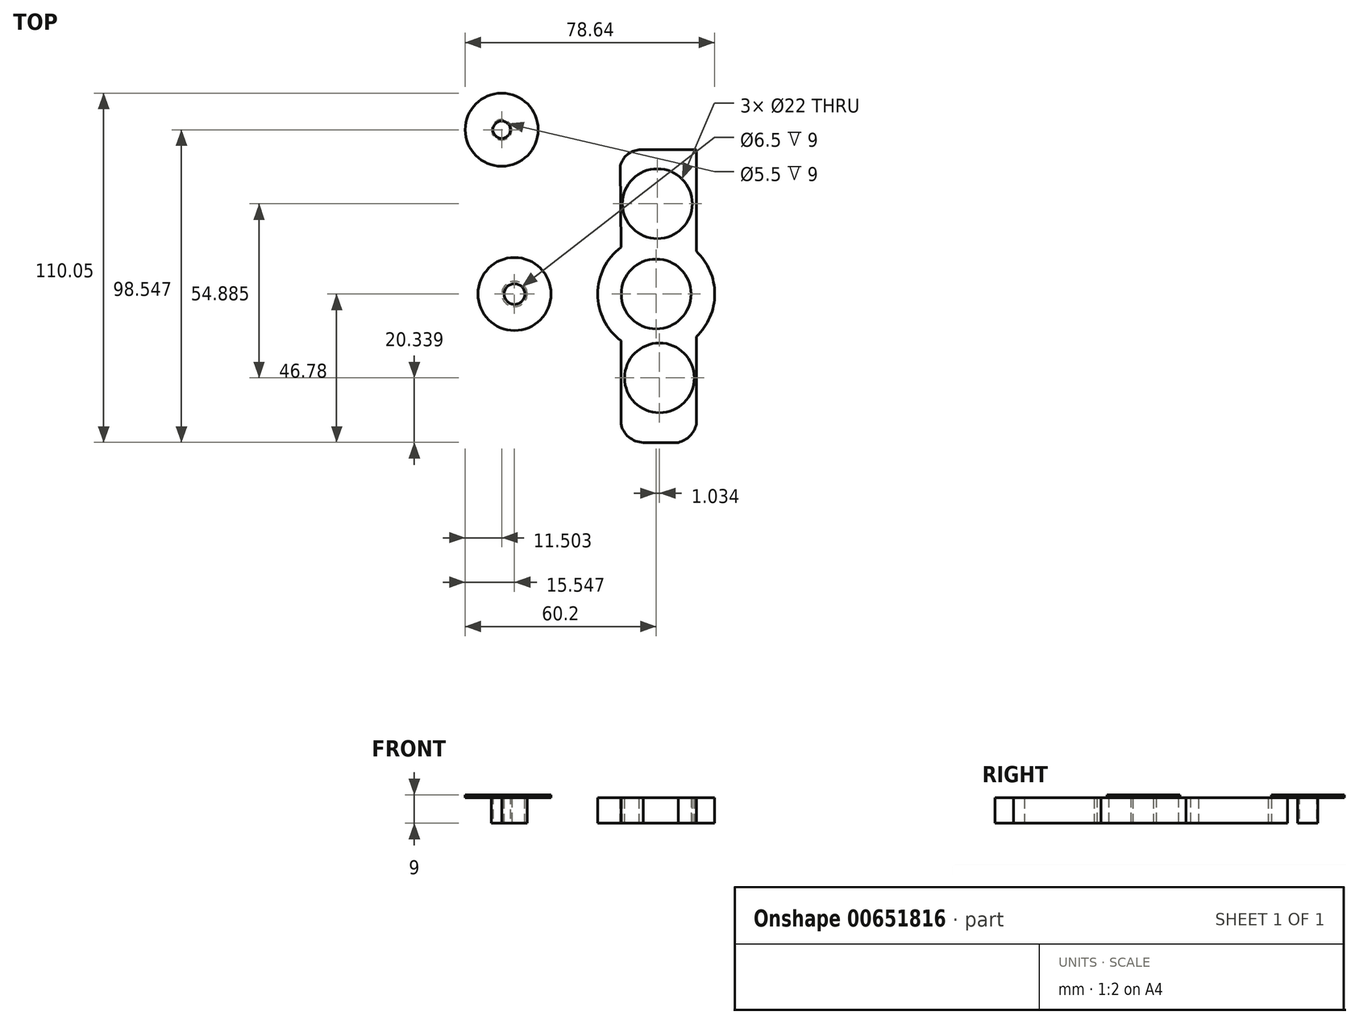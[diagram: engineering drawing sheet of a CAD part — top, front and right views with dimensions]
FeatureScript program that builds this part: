
annotation { "Feature Type Name" : "Feature", "Feature Type Description" : "" }
export const myFeature = defineFeature(function(context is Context, id is Id, definition is map)
    precondition{}
    {
        {
            var Q0;
            Q0=qCreatedBy(makeId("Top.planeOp"),FACE);
            var sketch = newSketch(context, id + "F0", { "sketchPlane" : qUnion([Q0])});
            skCircle(sketch, "E0", {"center": v(0, 0) * mm, "radius": 11 * mm});
            skCircle(sketch, "E1", {"center": v(0, 0) * mm, "radius": 18.44 * mm});
            skLineSegment(sketch, "E2", {"start": v(-11.12, 14.72) * mm, "end": v(-11.36, 45.43) * mm});
            skLineSegment(sketch, "E3", {"start": v(-11.36, 45.43) * mm, "end": v(12.64, 45.43) * mm});
            skLineSegment(sketch, "E4", {"start": v(12.64, 45.43) * mm, "end": v(12.64, 13.43) * mm});
            skLineSegment(sketch, "E5", {"start": v(-11.12, -14.72) * mm, "end": v(-11.12, -46.78) * mm});
            skLineSegment(sketch, "E6", {"start": v(12.64, -13.43) * mm, "end": v(12.64, -46.78) * mm});
            skLineSegment(sketch, "E7", {"start": v(12.64, -46.78) * mm, "end": v(-11.12, -46.78) * mm});
            skSolve(sketch);
        }
        {
            var Q0;
            {var subQ0=sQuery(id+"F0.wireOp",EDGE,"E2");Q0=makeQuery(id+"F0.imprint","IMPRINT",FACE,{"disambiguationData":[TD([[makeQuery(id+"F0.imprint","IMPRINT",EDGE,{"derivedFrom":subQ0}),-1.0]])]});}
            var Q1;
            Q1=makeQuery(id+"F0.imprint","IMPRINT",FACE,{"disambiguationData":[TD([[makeQuery(id+"F0.imprint","IMPRINT",EDGE,{"derivedFrom":sQuery(id+"F0.wireOp",EDGE,"E0")}),-1.0]])]});
            var Q2;
            {var subQ0=sQuery(id+"F0.wireOp",EDGE,"E5");Q2=makeQuery(id+"F0.imprint","IMPRINT",FACE,{"disambiguationData":[TD([[makeQuery(id+"F0.imprint","IMPRINT",EDGE,{"derivedFrom":subQ0}),1.0]])]});}
            extrude(context, id + "F1", {"entities" : qUnion([Q0, Q1, Q2]), "depth" : 8 * mm});
        }
        {
            var Q0;
            Q0=makeQuery(id+"F1.opExtrude","CAP_FACE",FACE,{"disambiguationData":[OSD([sQuery(id+"F0.wireOp",EDGE,"E0"),sQuery(id+"F0.wireOp",EDGE,"E1"),sQuery(id+"F0.wireOp",EDGE,"E2"),sQuery(id+"F0.wireOp",EDGE,"E3"),sQuery(id+"F0.wireOp",EDGE,"E4"),sQuery(id+"F0.wireOp",EDGE,"E5"),sQuery(id+"F0.wireOp",EDGE,"E6"),sQuery(id+"F0.wireOp",EDGE,"E7")])],"isStart":false});
            var sketch = newSketch(context, id + "F2", { "sketchPlane" : qUnion([Q0])});
            skArc(sketch, "E8", {"start": v(-11.12, -37.97) * mm, "mid": v(-9.67, -44) * mm, "end": v(-4.13, -46.78) * mm});
            skArc(sketch, "E9", {"start": v(6.95, -46.78) * mm, "mid": v(11.59, -43.53) * mm, "end": v(12.64, -37.97) * mm});
            skArc(sketch, "E10", {"start": v(12.64, 37.03) * mm, "mid": v(11.6, 43.27) * mm, "end": v(5.64, 45.43) * mm});
            skArc(sketch, "E11", {"start": v(-4.13, 45.43) * mm, "mid": v(-9.92, 43.1) * mm, "end": v(-11.36, 37.03) * mm});
            skSolve(sketch);
        }
        {
            var Q0;
            {var subQ0=sQuery(id+"F2.wireOp",EDGE,"E11");var subQ1=makeQuery(id+"F1.opExtrude","CAP_EDGE",EDGE,{"disambiguationData":[OSD([sQuery(id+"F0.wireOp",EDGE,"E2")])],"isStart":false});var subQ2=makeQuery(id+"F2.imprint","INTERSECT",VERTEX,{"derivedFrom":[subQ1,subQ0]});Q0=makeQuery(id+"F2.imprint","IMPRINT",FACE,{"disambiguationData":[TD([[makeQuery(id+"F2.imprint","IMPRINT",EDGE,{"disambiguationData":[TD([[subQ2,1.0]])],"derivedFrom":subQ0}),-1.0]])]});}
            var Q1;
            {var subQ0=sQuery(id+"F2.wireOp",EDGE,"E10");var subQ1=makeQuery(id+"F1.opExtrude","CAP_EDGE",EDGE,{"disambiguationData":[OSD([sQuery(id+"F0.wireOp",EDGE,"E4")])],"isStart":false});var subQ2=makeQuery(id+"F2.imprint","INTERSECT",VERTEX,{"disambiguationData":[OD(1.0)],"derivedFrom":[subQ1,subQ0]});Q1=makeQuery(id+"F2.imprint","IMPRINT",FACE,{"disambiguationData":[TD([[makeQuery(id+"F2.imprint","IMPRINT",EDGE,{"disambiguationData":[TD([[subQ2,-1.0]])],"derivedFrom":subQ0}),-1.0]])]});}
            var Q2;
            {var subQ0=sQuery(id+"F2.wireOp",EDGE,"E8");var subQ1=makeQuery(id+"F1.opExtrude","CAP_EDGE",EDGE,{"disambiguationData":[OSD([sQuery(id+"F0.wireOp",EDGE,"E7")])],"isStart":false});var subQ2=makeQuery(id+"F2.imprint","INTERSECT",VERTEX,{"derivedFrom":[subQ1,subQ0]});Q2=makeQuery(id+"F2.imprint","IMPRINT",FACE,{"disambiguationData":[TD([[makeQuery(id+"F2.imprint","IMPRINT",EDGE,{"disambiguationData":[TD([[subQ2,1.0]])],"derivedFrom":subQ0}),-1.0]])]});}
            var Q3;
            {var subQ0=sQuery(id+"F2.wireOp",EDGE,"E9");var subQ1=makeQuery(id+"F1.opExtrude","CAP_EDGE",EDGE,{"disambiguationData":[OSD([sQuery(id+"F0.wireOp",EDGE,"E7")])],"isStart":false});var subQ2=makeQuery(id+"F2.imprint","INTERSECT",VERTEX,{"derivedFrom":[subQ1,subQ0]});Q3=makeQuery(id+"F2.imprint","IMPRINT",FACE,{"disambiguationData":[TD([[makeQuery(id+"F2.imprint","IMPRINT",EDGE,{"disambiguationData":[TD([[subQ2,-1.0]])],"derivedFrom":subQ0}),-1.0]])]});}
            extrude(context, id + "F3", {"entities" : qUnion([Q0, Q1, Q2, Q3]), "operationType" : NewBodyOperationType.REMOVE, "oppositeDirection" : true, "depth" : 25 * mm});
        }
        {
            var Q0;
            Q0=qCreatedBy(makeId("Top.planeOp"),FACE);
            var sketch = newSketch(context, id + "F4", { "sketchPlane" : qUnion([Q0])});
            skCircle(sketch, "E12", {"center": v(-44.65, 0) * mm, "radius": 4 * mm});
            skSolve(sketch);
        }
        {
            var Q0;
            Q0=makeQuery(id+"F4.imprint","IMPRINT",FACE,{"disambiguationData":[TD([[makeQuery(id+"F4.imprint","IMPRINT",EDGE,{"derivedFrom":sQuery(id+"F4.wireOp",EDGE,"E12")}),1.0]])]});
            extrude(context, id + "F5", {"entities" : qUnion([Q0]), "depth" : 8 * mm});
        }
        {
            var Q0;
            Q0=makeQuery(id+"F5.opExtrude","CAP_FACE",FACE,{"disambiguationData":[OSD([sQuery(id+"F4.wireOp",EDGE,"E12")])],"isStart":false});
            var sketch = newSketch(context, id + "F6", { "sketchPlane" : qUnion([Q0])});
            skCircle(sketch, "E13", {"center": v(-44.65, 0) * mm, "radius": 3.25 * mm});
            skSolve(sketch);
        }
        {
            var Q0;
            Q0=makeQuery(id+"F6.imprint","IMPRINT",FACE,{"disambiguationData":[TD([[makeQuery(id+"F6.imprint","IMPRINT",EDGE,{"derivedFrom":sQuery(id+"F6.wireOp",EDGE,"E13")}),1.0]])]});
            extrude(context, id + "F7", {"entities" : qUnion([Q0]), "operationType" : NewBodyOperationType.REMOVE, "oppositeDirection" : true, "depth" : 25 * mm});
        }
        {
            var Q0;
            Q0=makeQuery(id+"F5.opExtrude","CAP_FACE",FACE,{"disambiguationData":[OSD([sQuery(id+"F4.wireOp",EDGE,"E12")])],"isStart":false});
            var sketch = newSketch(context, id + "F8", { "sketchPlane" : qUnion([Q0])});
            skCircle(sketch, "E14", {"center": v(-44.65, 0) * mm, "radius": 11.5 * mm});
            skSolve(sketch);
        }
        {
            var Q0;
            Q0=qSketchRegion(id+"F8",true);
            extrude(context, id + "F9", {"entities" : qUnion([Q0]), "operationType" : NewBodyOperationType.ADD, "depth" : 1 * mm});
        }
        {
            var Q0;
            Q0=makeQuery(id+"F9.boolean.opBoolean","SPLIT",FACE,{"disambiguationData":[TD([makeQuery(id+"F7.boolean.opBoolean","COPY",FACE,{"derivedFrom":makeQuery(id+"F7.opExtrude","SWEPT_FACE",FACE,{"disambiguationData":[OSD([sQuery(id+"F6.wireOp",EDGE,"E13")])]})})])],"derivedFrom":makeQuery(id+"F9.opExtrude","CAP_FACE",FACE,{"disambiguationData":[OSD([sQuery(id+"F8.wireOp",EDGE,"E14")])],"isStart":true})});
            var sketch = newSketch(context, id + "F10", { "sketchPlane" : qUnion([Q0])});
            skCircle(sketch, "E15", {"center": v(-44.65, 0) * mm, "radius": 3.25 * mm});
            skSolve(sketch);
        }
        {
            var Q0;
            Q0=qSketchRegion(id+"F10",true);
            extrude(context, id + "F11", {"entities" : qUnion([Q0]), "operationType" : NewBodyOperationType.REMOVE, "oppositeDirection" : true, "depth" : 25 * mm});
        }
        {
            var Q0;
            Q0=qCreatedBy(makeId("Top.planeOp"),FACE);
            var sketch = newSketch(context, id + "F12", { "sketchPlane" : qUnion([Q0])});
            skCircle(sketch, "E16", {"center": v(-48.7, 51.77) * mm, "radius": 3.2 * mm});
            skSolve(sketch);
        }
        {
            var Q0;
            Q0=makeQuery(id+"F12.imprint","IMPRINT",FACE,{"disambiguationData":[TD([[makeQuery(id+"F12.imprint","IMPRINT",EDGE,{"derivedFrom":sQuery(id+"F12.wireOp",EDGE,"E16")}),1.0]])]});
            extrude(context, id + "F13", {"entities" : qUnion([Q0]), "depth" : 8 * mm});
        }
        {
            var Q0;
            Q0=makeQuery(id+"F13.opExtrude","CAP_FACE",FACE,{"disambiguationData":[OSD([sQuery(id+"F12.wireOp",EDGE,"E16")])],"isStart":false});
            var sketch = newSketch(context, id + "F14", { "sketchPlane" : qUnion([Q0])});
            skCircle(sketch, "E17", {"center": v(-48.7, 51.77) * mm, "radius": 11.5 * mm});
            skSolve(sketch);
        }
        {
            var Q0;
            Q0=qSketchRegion(id+"F14",true);
            var Q1;
            Q1=makeQuery(id+"F14.imprint","IMPRINT",FACE,{"disambiguationData":[TD([[makeQuery(id+"F14.imprint","IMPRINT",EDGE,{"derivedFrom":makeQuery(id+"F13.opExtrude","CAP_EDGE",EDGE,{"disambiguationData":[OSD([sQuery(id+"F12.wireOp",EDGE,"E16")])],"isStart":false})}),1.0]])]});
            extrude(context, id + "F15", {"entities" : qUnion([Q0, Q1]), "operationType" : NewBodyOperationType.ADD, "depth" : 1 * mm});
        }
        {
            var Q0;
            Q0=makeQuery(id+"F13.opExtrude","CAP_FACE",FACE,{"disambiguationData":[OSD([sQuery(id+"F12.wireOp",EDGE,"E16")])],"isStart":true});
            var sketch = newSketch(context, id + "F16", { "sketchPlane" : qUnion([Q0])});
            skCircle(sketch, "E18", {"center": v(-48.7, -51.77) * mm, "radius": 2.75 * mm});
            skSolve(sketch);
        }
        {
            var Q0;
            Q0=makeQuery(id+"F16.imprint","IMPRINT",FACE,{"disambiguationData":[TD([[makeQuery(id+"F16.imprint","IMPRINT",EDGE,{"derivedFrom":sQuery(id+"F16.wireOp",EDGE,"E18")}),1.0]])]});
            extrude(context, id + "F17", {"entities" : qUnion([Q0]), "operationType" : NewBodyOperationType.REMOVE, "oppositeDirection" : true, "depth" : 25 * mm});
        }
        {
            var Q0;
            Q0=makeQuery(id+"F1.opExtrude","CAP_FACE",FACE,{"disambiguationData":[OSD([sQuery(id+"F0.wireOp",EDGE,"E0"),sQuery(id+"F0.wireOp",EDGE,"E1"),sQuery(id+"F0.wireOp",EDGE,"E2"),sQuery(id+"F0.wireOp",EDGE,"E3"),sQuery(id+"F0.wireOp",EDGE,"E4"),sQuery(id+"F0.wireOp",EDGE,"E5"),sQuery(id+"F0.wireOp",EDGE,"E6"),sQuery(id+"F0.wireOp",EDGE,"E7")])],"isStart":false});
            var sketch = newSketch(context, id + "F18", { "sketchPlane" : qUnion([Q0])});
            skCircle(sketch, "E19", {"center": v(1.03, -26.44) * mm, "radius": 11 * mm});
            skCircle(sketch, "E20", {"center": v(0.38, 28.44) * mm, "radius": 11 * mm});
            skSolve(sketch);
        }
        {
            var Q0;
            Q0=qSketchRegion(id+"F18",true);
            extrude(context, id + "F19", {"entities" : qUnion([Q0]), "operationType" : NewBodyOperationType.REMOVE, "oppositeDirection" : true, "depth" : 25 * mm});
        }
    });
